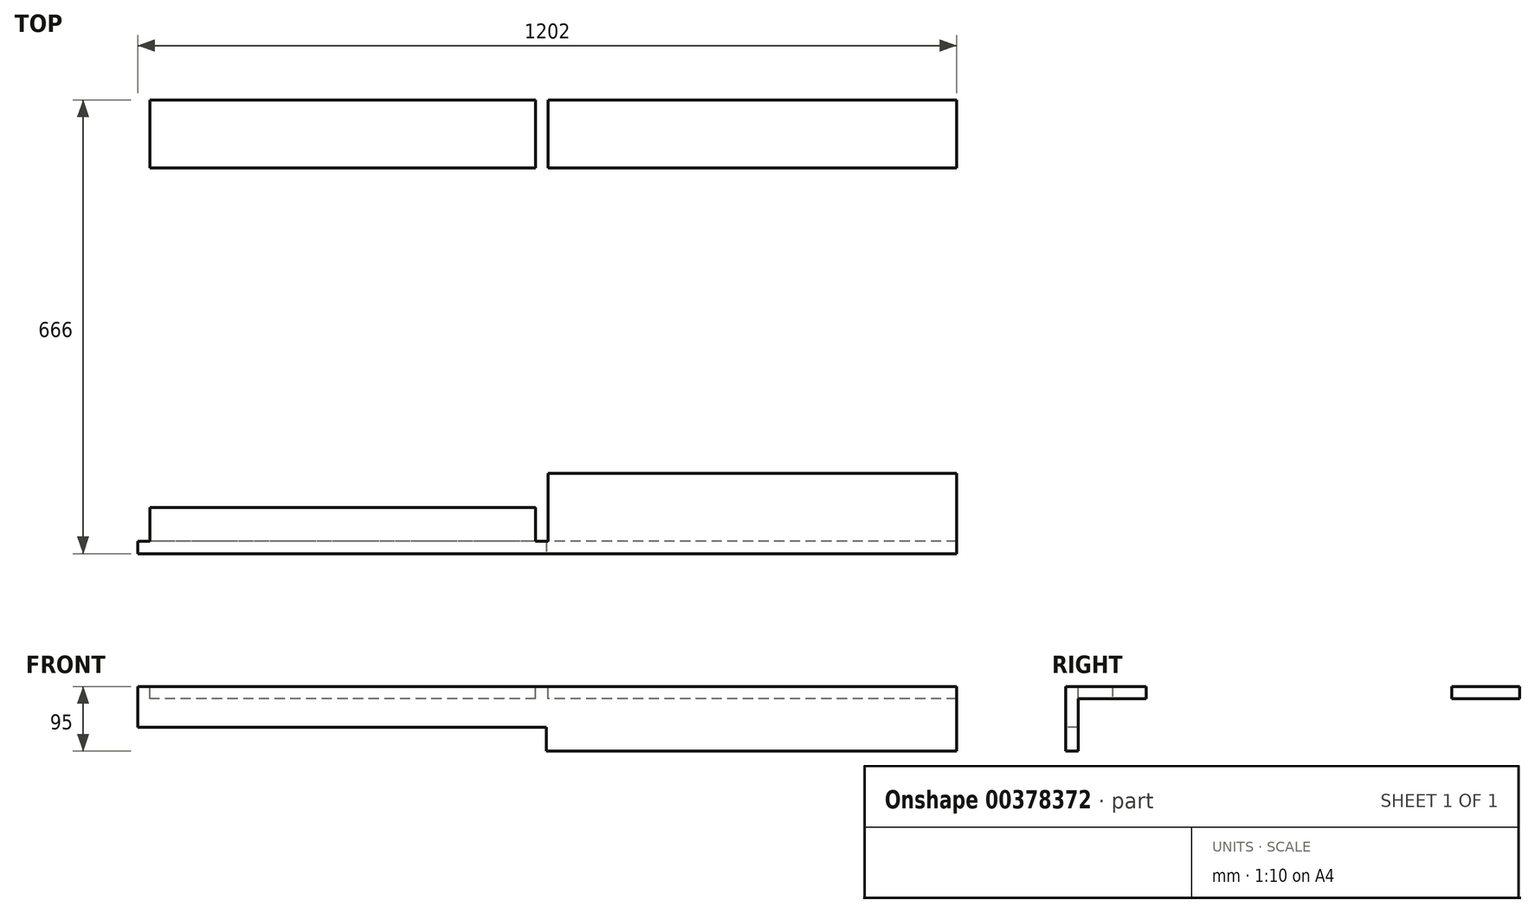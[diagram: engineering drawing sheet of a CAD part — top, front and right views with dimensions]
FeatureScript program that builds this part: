
annotation { "Feature Type Name" : "Feature", "Feature Type Description" : "" }
export const myFeature = defineFeature(function(context is Context, id is Id, definition is map)
    precondition{}
    {
        {
            var Q0;
            Q0=qCreatedBy(makeId("Right.planeOp"),FACE);
            var sketch = newSketch(context, id + "F0", { "sketchPlane" : qUnion([Q0])});
            skLineSegment(sketch, "E0.bottom", {"start": v(322.27, 0) * mm, "end": v(422.27, 0) * mm});
            skLineSegment(sketch, "E0.top", {"start": v(322.27, -18) * mm, "end": v(422.27, -18) * mm});
            skLineSegment(sketch, "E0.left", {"start": v(322.27, 0) * mm, "end": v(322.27, -18) * mm});
            skLineSegment(sketch, "E0.right", {"start": v(422.27, 0) * mm, "end": v(422.27, -18) * mm});
            skLineSegment(sketch, "E1.bottom", {"start": v(-125.73, 0) * mm, "end": v(-243.73, 0) * mm});
            skLineSegment(sketch, "E1.top", {"start": v(-125.73, -18) * mm, "end": v(-225.73, -18) * mm});
            skLineSegment(sketch, "E1.left", {"start": v(-125.73, 0) * mm, "end": v(-125.73, -18) * mm});
            skLineSegment(sketch, "E2.top", {"start": v(-225.73, -95) * mm, "end": v(-243.73, -95) * mm});
            skLineSegment(sketch, "E2.left", {"start": v(-225.73, -18) * mm, "end": v(-225.73, -95) * mm});
            skLineSegment(sketch, "E2.right", {"start": v(-243.73, 0) * mm, "end": v(-243.73, -95) * mm});
            skSolve(sketch);
        }
        {
            var Q0;
            Q0 = qSketchRegion(id + "F0", true);
            extrude(context, id + "F1", {"entities" : qUnion([Q0]), "depth" : 1202 * mm});
        }
        {
            var Q0;
            Q0=makeQuery(id+"F1.opExtrude","SWEPT_FACE",FACE,{"disambiguationData":[OSD([sQuery(id+"F0.wireOp",EDGE,"E1.bottom")])]});
            var sketch = newSketch(context, id + "F2", { "sketchPlane" : qUnion([Q0])});
            skLineSegment(sketch, "E3.bottom", {"start": v(584, 422.27) * mm, "end": v(602, 422.27) * mm});
            skLineSegment(sketch, "E3.top", {"start": v(584, -225.73) * mm, "end": v(602, -225.73) * mm});
            skLineSegment(sketch, "E3.left", {"start": v(584, 422.27) * mm, "end": v(584, -225.73) * mm});
            skLineSegment(sketch, "E3.right", {"start": v(602, 422.27) * mm, "end": v(602, -225.73) * mm});
            skLineSegment(sketch, "E4.bottom", {"start": v(0, 422.27) * mm, "end": v(18, 422.27) * mm});
            skLineSegment(sketch, "E4.top", {"start": v(0, -225.73) * mm, "end": v(18, -225.73) * mm});
            skLineSegment(sketch, "E4.left", {"start": v(0, 422.27) * mm, "end": v(0, -225.73) * mm});
            skLineSegment(sketch, "E4.right", {"start": v(18, 422.27) * mm, "end": v(18, -225.73) * mm});
            skSolve(sketch);
        }
        {
            var Q0;
            Q0 = qSketchRegion(id + "F2", true);
            extrude(context, id + "F3", {"entities" : qUnion([Q0]), "operationType" : NewBodyOperationType.REMOVE, "oppositeDirection" : true, "depth" : 95 * mm});
        }
        {
            var Q0;
            Q0=makeQuery(id+"F1.opExtrude","SWEPT_FACE",FACE,{"disambiguationData":[OSD([sQuery(id+"F0.wireOp",EDGE,"E2.right")])]});
            var sketch = newSketch(context, id + "F4", { "sketchPlane" : qUnion([Q0])});
            skLineSegment(sketch, "E5.bottom", {"start": v(0, -95) * mm, "end": v(600, -95) * mm});
            skLineSegment(sketch, "E5.top", {"start": v(0, -60) * mm, "end": v(600, -60) * mm});
            skLineSegment(sketch, "E5.left", {"start": v(0, -95) * mm, "end": v(0, -60) * mm});
            skLineSegment(sketch, "E5.right", {"start": v(600, -95) * mm, "end": v(600, -60) * mm});
            skSolve(sketch);
        }
        {
            var Q0;
            Q0 = qSketchRegion(id + "F4", true);
            extrude(context, id + "F5", {"entities" : qUnion([Q0]), "operationType" : NewBodyOperationType.REMOVE, "oppositeDirection" : true, "depth" : 25 * mm});
        }
        {
            var Q0;
            Q0=makeQuery(id+"F1.opExtrude","SWEPT_FACE",FACE,{"disambiguationData":[OSD([sQuery(id+"F0.wireOp",EDGE,"E1.bottom")])]});
            var sketch = newSketch(context, id + "F6", { "sketchPlane" : qUnion([Q0])});
            skLineSegment(sketch, "E6.bottom", {"start": v(602, -125.73) * mm, "end": v(-21.87, -125.73) * mm});
            skLineSegment(sketch, "E6.top", {"start": v(602, -175.73) * mm, "end": v(-21.87, -175.73) * mm});
            skLineSegment(sketch, "E6.left", {"start": v(602, -125.73) * mm, "end": v(602, -175.73) * mm});
            skLineSegment(sketch, "E6.right", {"start": v(-21.87, -125.73) * mm, "end": v(-21.87, -175.73) * mm});
            skLineSegment(sketch, "E7.bottom", {"start": v(18, -125.73) * mm, "end": v(584, -125.73) * mm});
            skLineSegment(sketch, "E7.top", {"start": v(18, -175.73) * mm, "end": v(584, -175.73) * mm});
            skLineSegment(sketch, "E7.left", {"start": v(18, -125.73) * mm, "end": v(18, -175.73) * mm});
            skLineSegment(sketch, "E7.right", {"start": v(584, -125.73) * mm, "end": v(584, -175.73) * mm});
            skSolve(sketch);
        }
        {
            var Q0;
            Q0 = qSketchRegion(id + "F6", true);
            extrude(context, id + "F7", {"entities" : qUnion([Q0]), "operationType" : NewBodyOperationType.REMOVE, "oppositeDirection" : true, "depth" : 18 * mm});
        }
    });
